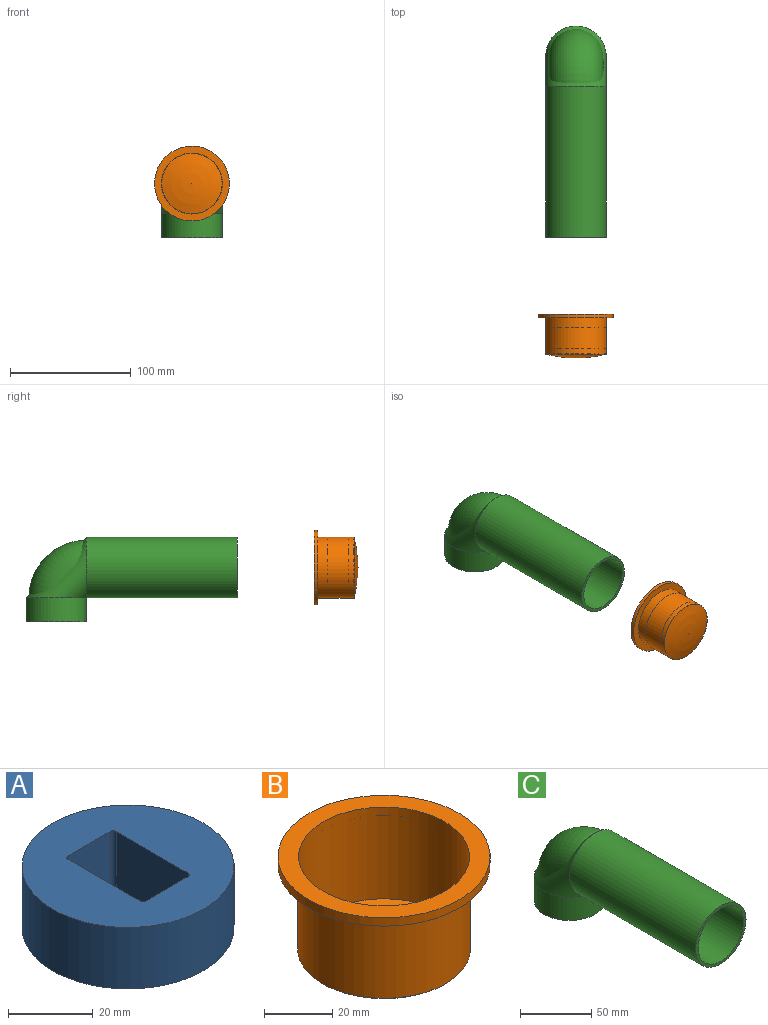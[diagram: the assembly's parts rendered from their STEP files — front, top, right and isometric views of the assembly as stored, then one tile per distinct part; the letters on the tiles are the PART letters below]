
ASSEMBLY  parts=3 mates=2
PART A: 11 faces, bbox 50x50x17.8 mm
  f0: plane 24x17.75mm, normal (1,0,0), area 426mm2, adj f5,f6,f7,f9
  f1: plane 17.75x14mm, normal (0,-1,0), area 248.5mm2, adj f5,f6,f7,f8
  f2: plane 24x17.75mm, normal (-1,0,0), area 426mm2, adj f5,f6,f8,f10
  f3: plane 17.75x14mm, normal (0,1,0), area 248.5mm2, adj f5,f6,f9,f10
  f4: cylinder r=25mm len=50mm, axis (0,0,-1), area 2788.2mm2, adj f5,f6
  f5: plane 50x50mm, normal (0,0,1), area 1548.4mm2, adj f0,f1,f2,f3,f4,f7,f8,f9
  f6: plane 50x50mm, normal (0,0,-1), area 1548.4mm2, adj f0,f1,f2,f3,f4,f7,f8,f9
  f7: cylinder r=1mm len=17.75mm, axis (0,0,-1), area 27.9mm2, adj f0,f1,f5,f6
  f8: cylinder r=1mm len=17.75mm, axis (0,0,1), area 27.9mm2, adj f1,f2,f5,f6
  f9: cylinder r=1mm len=17.75mm, axis (0,0,1), area 27.9mm2, adj f0,f3,f5,f6
  f10: cylinder r=1mm len=17.75mm, axis (0,0,-1), area 27.9mm2, adj f2,f3,f5,f6
PART B: 7 faces, bbox 62x62x36.2 mm
  f0: sphere r=100mm, area 2035.9mm2, adj f1
  f1: cylinder r=25.25mm len=50.5mm, axis (0,0,1), area 4759.5mm2, adj f0,f2
  f2: plane 62x62mm, normal (0,0,-1), area 1016.1mm2, adj f1,f3
  f3: cylinder r=31mm len=62mm, axis (0,0,1), area 584.3mm2, adj f2,f4
  f4: plane 62x62mm, normal (0,0,1), area 1055.6mm2, adj f3,f5
  f5: cylinder r=25mm len=50mm, axis (0,0,1), area 5154.6mm2, adj f4,f6
  f6: sphere r=100mm, area 1995.2mm2, adj f5
PART C: 8 faces, bbox 50x179.1x74.1 mm
  f0: plane 50x50mm, normal (0,-1,0), area 373.1mm2, adj f2,f5
  f1: plane 50x50mm, normal (0,0,-1), area 373.1mm2, adj f4,f7
  f2: cylinder r=25mm len=125mm, axis (0,1,0), area 19635mm2, adj f0,f3
  f3: torus R=25mm, axis (-1,0,0), area 6168.5mm2, adj f2,f4
  f4: cylinder r=25mm len=50mm, axis (0,0,-1), area 3141.6mm2, adj f1,f3
  f5: cylinder r=22.5mm len=125mm, axis (0,1,0), area 17671.5mm2, adj f0,f6
  f6: torus R=25mm, axis (-1,0,0), area 5551.7mm2, adj f5,f7
  f7: cylinder r=22.5mm len=45mm, axis (0,0,-1), area 2827.4mm2, adj f1,f6
PLACE A rot(axis=(-1,0,0),90deg) t=(-8.9,-81.53,-3.34)mm
PLACE B rot(axis=(-1,0,0),90deg) t=(-8.9,-88.9,-3.34)mm
PLACE C t=(-8.9,10.98,-3.34)mm
MATE fastened B.f1 <-> A.f4  axis (0,1,0) through (-8.9,-55.78,-3.34)mm
MATE fastened B.f1 <-> C.f2  axis (0,1,0) through (-8.9,10.98,-3.34)mm
